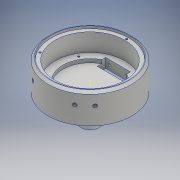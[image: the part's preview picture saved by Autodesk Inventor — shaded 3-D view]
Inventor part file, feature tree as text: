
AUTODESK INVENTOR PART (.ipt)
format: ipt  version: 2017 (Build 210142000, 142)  size: 281,600 bytes
history: native  units: mm
features: sketch x14, thread x10, extrude x7, hole x7, plane x6, projected_geometry x2, chamfer x1
ambient origin geometry x8: Origin, YZ Plane, XZ Plane, XY Plane, X Axis, Y Axis, Z Axis, Center Point
bodies: Solid1 (feature_tree)
feature tree (47):
  extrude  "Extrusion1"  Depth=25.0mm TaperAngle=0.0deg
  extrude  "Extrusion2"  Depth=17.0mm TaperAngle=0.0deg
  extrude  "Extrusion4"  Depth=35.0mm
  plane  "Work Plane1"
  extrude  "Extrusion7"  Depth=2.0mm TaperAngle=0.0deg
  chamfer  "Chamfer1"  Distance=2.0mm Angle=45.0deg
  hole  "Hole3"  [1 undecoded]
  hole  "Hole4"  [1 undecoded]
  thread  "Thread1"  [1 undecoded]
  thread  "Thread2"  [1 undecoded]
  thread  "Thread3"  [1 undecoded]
  thread  "Thread4"  [1 undecoded]
  thread  "Thread5"  [1 undecoded]
  thread  "Thread6"  [1 undecoded]
  sketch  "Sketch12"  dims[d54=1.6mm d55=6.0mm d56=4.0mm d57=2.0mm d58=90.0deg d59=5.0mm d60=20.594885mm d61=61.315mm d62=30.0mm d64=360.0deg]
  plane  "Work Plane2"
  plane  "Work Plane3"
  plane  "Work Plane4"
  plane  "Work Plane5"
  hole  "Hole5"  [1 undecoded]
  hole  "Hole6"  [1 undecoded]
  hole  "Hole9"  [1 undecoded]
  hole  "Hole10"  [1 undecoded]
  thread  "Thread7"  [1 undecoded]
  thread  "Thread8"  [1 undecoded]
  extrude  "Extrusion8"  Depth=14.5mm
  thread  "Thread11"  [1 undecoded]
  thread  "Thread12"  [1 undecoded]
  sketch  "Sketch21"  dims[d88=3.0mm d89=6.0mm d90=4.0mm d91=2.0mm d92=90.0deg d93=4.0mm d94=20.594885mm d95=14.5mm]
  sketch  "Sketch22"  dims[d96=3.0mm d97=6.0mm d98=4.0mm d99=2.0mm d100=90.0deg d101=4.0mm d102=20.594885mm d117=10.0mm d118=0.0mm d119=10.0mm d120=0.0mm d125=15.0mm]
  extrude  "Extrusion10"  Depth=10.0mm TaperAngle=0.0deg
  hole  "Hole12"  [1 undecoded]
  plane  "Work Plane7"
  extrude  "Extrusion11"  Depth=5.0mm
  sketch  "Sketch1"  dims[d0=70.0mm d1=25.0mm d2=0.0mm]
  sketch  "Sketch2"  dims[d3=47.0mm d8=17.0mm d9=0.0mm]
  sketch  "Sketch8"  dims[d13=3.0mm d14=0.0mm d32=35.0mm]
  sketch  "Sketch10"  dims[d36=65.0mm d37=2.0mm d38=0.0mm d46=2.0mm d47=2.0mm d48=45.0deg]
  projected_geometry  "Projected Loop4"
  sketch  "Sketch11"  dims[d49=51.762mm d50=30.0mm d52=360.0deg]
  sketch  "Sketch13"  dims[d66=1.6mm d67=6.0mm d68=4.0mm d69=2.0mm d70=90.0deg d71=5.0mm d72=20.594885mm d73=10.0mm d74=0.0mm d75=10.0mm d76=0.0mm d77=10.0mm d78=0.0mm d79=10.0mm d80=0.0mm d81=10.0mm d82=0.0mm]
  sketch  "Sketch14"  dims[d83=10.0mm d84=0.0mm d85=6.981317mm]
  sketch  "Sketch17"  dims[d86=60.0deg d87=14.5mm]
  sketch  "Sketch23"  dims[d126=22.2mm d127=0.0mm d128=14.5mm d129=14.5mm]
  sketch  "Sketch24"  dims[d130=3.0mm d131=6.0mm d132=4.0mm d133=2.0mm d134=90.0deg d135=4.0mm d136=20.594885mm]
  sketch  "Sketch25"  dims[d137=3.0mm d138=6.0mm d139=4.0mm d140=2.0mm d141=90.0deg d142=4.0mm d143=20.594885mm d144=10.0mm d145=0.0mm d146=10.0mm d147=0.0mm d148=45.762433mm d173=58.5mm d175=47.2mm d176=21.0mm d177=7.0mm d178=10.0mm d179=0.0mm d180=15.0mm d181=2.1mm d182=2.1mm d183=4.1mm d184=4.1mm d185=7.5mm d186=7.5mm d187=2.1mm d188=6.0mm d189=4.0mm d190=2.0mm d191=90.0deg d192=8.0mm d193=20.594885mm d194=35.0mm d195=5.0mm d196=2.0mm d197=0.0mm d172=1.0mm]
  projected_geometry  "Projected Loop6"
note: 17 required parameter values undecoded (feature->parameter linkage not recoverable at this tier; creation-order binding heuristic only, values carry confidence <= 0.55)
